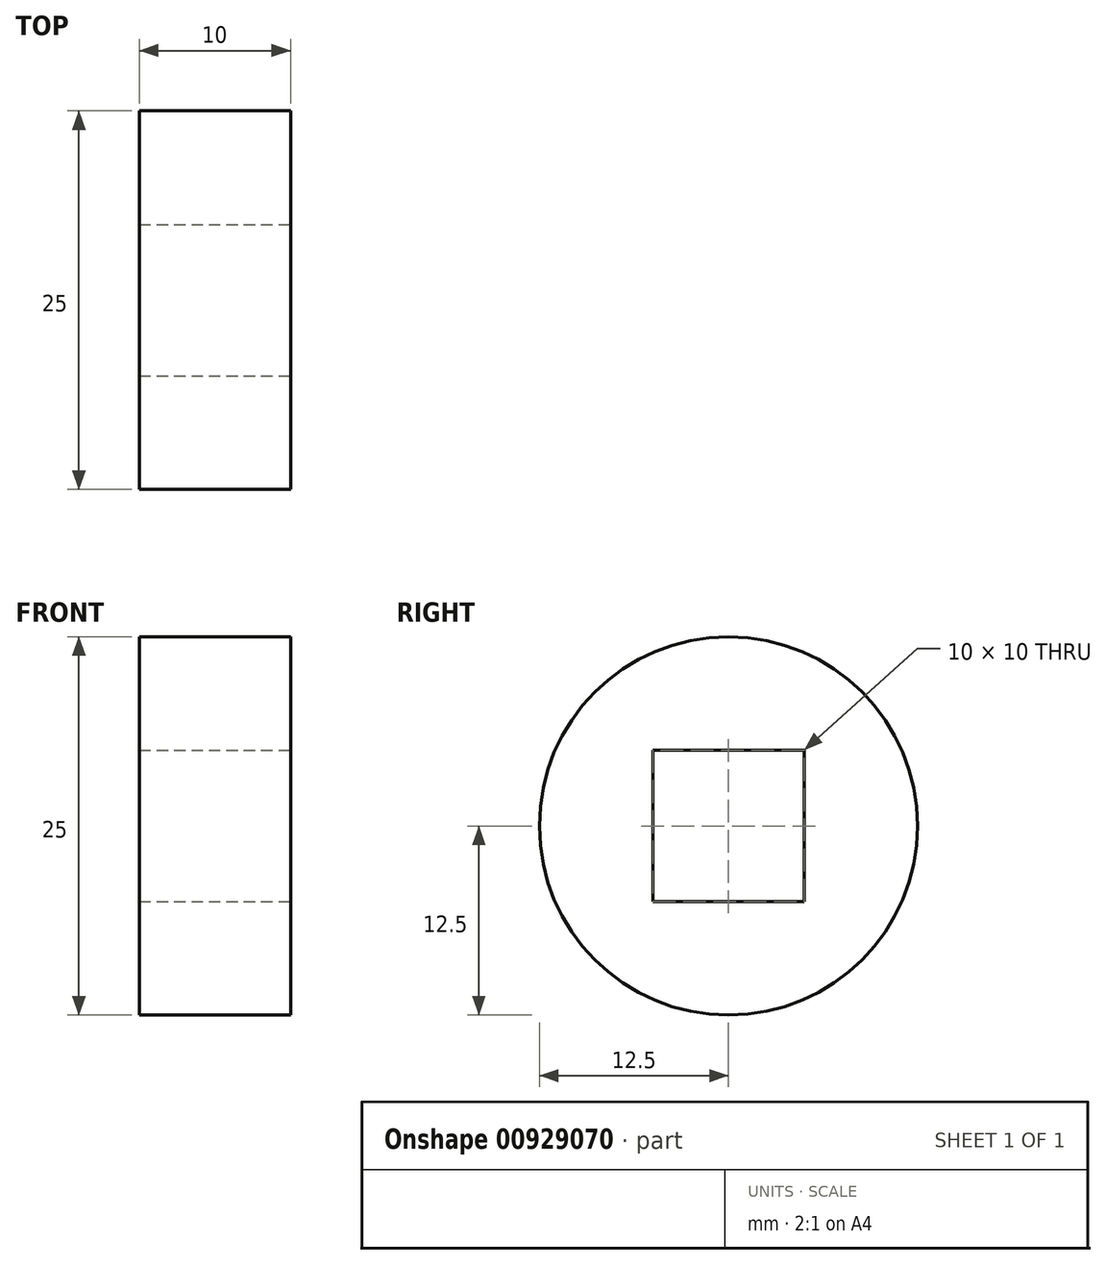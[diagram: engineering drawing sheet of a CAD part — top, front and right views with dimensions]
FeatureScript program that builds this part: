
annotation { "Feature Type Name" : "Feature", "Feature Type Description" : "" }
export const myFeature = defineFeature(function(context is Context, id is Id, definition is map)
    precondition{}
    {
        {
            var Q0;
            Q0=qCreatedBy(makeId("Right.planeOp"),FACE);
            var sketch = newSketch(context, id + "F0", { "sketchPlane" : qUnion([Q0])});
            skCircle(sketch, "E0", {"center": v(0, 0) * mm, "radius": 12.5 * mm});
            skLineSegment(sketch, "E1", {"start": v(0, 0) * mm, "end": v(0, 0) * mm});
            skCircle(sketch, "E2", {"center": v(0, 0) * mm, "radius": 25 * mm, "construction": true});
            skSolve(sketch);
        }
        {
            var Q0;
            Q0=qCreatedBy(makeId("Right.planeOp"),FACE);
            var sketch = newSketch(context, id + "F1", { "sketchPlane" : qUnion([Q0])});
            skLineSegment(sketch, "E3.bottom", {"start": v(5, 5) * mm, "end": v(-5, 5) * mm});
            skLineSegment(sketch, "E3.top", {"start": v(5, -5) * mm, "end": v(-5, -5) * mm});
            skLineSegment(sketch, "E3.left", {"start": v(5, 5) * mm, "end": v(5, -5) * mm});
            skLineSegment(sketch, "E3.right", {"start": v(-5, 5) * mm, "end": v(-5, -5) * mm});
            skPoint(sketch, "E3.middle", {"position": v(0, 0) * mm});
            skSolve(sketch);
        }
        {
            var Q0;
            Q0=qSketchRegion(id+"F0",true);
            extrude(context, id + "F2", {"entities" : qUnion([Q0]), "endBound" : BoundingType.SYMMETRIC, "depth" : 10 * mm, "offsetDistance" : 25 * mm});
        }
        {
            var Q0;
            Q0 = qSketchRegion(id + "F1", true);
            extrude(context, id + "F3", {"entities" : qUnion([Q0]), "operationType" : NewBodyOperationType.REMOVE, "endBound" : BoundingType.THROUGH_ALL, "oppositeDirection" : true, "depth" : 25 * mm, "offsetDistance" : 25 * mm, "hasSecondDirection" : true, "secondDirectionBound" : SecondDirectionBoundingType.THROUGH_ALL, "secondDirectionOppositeDirection" : false, "secondDirectionDepth" : 25 * mm});
        }
    });
